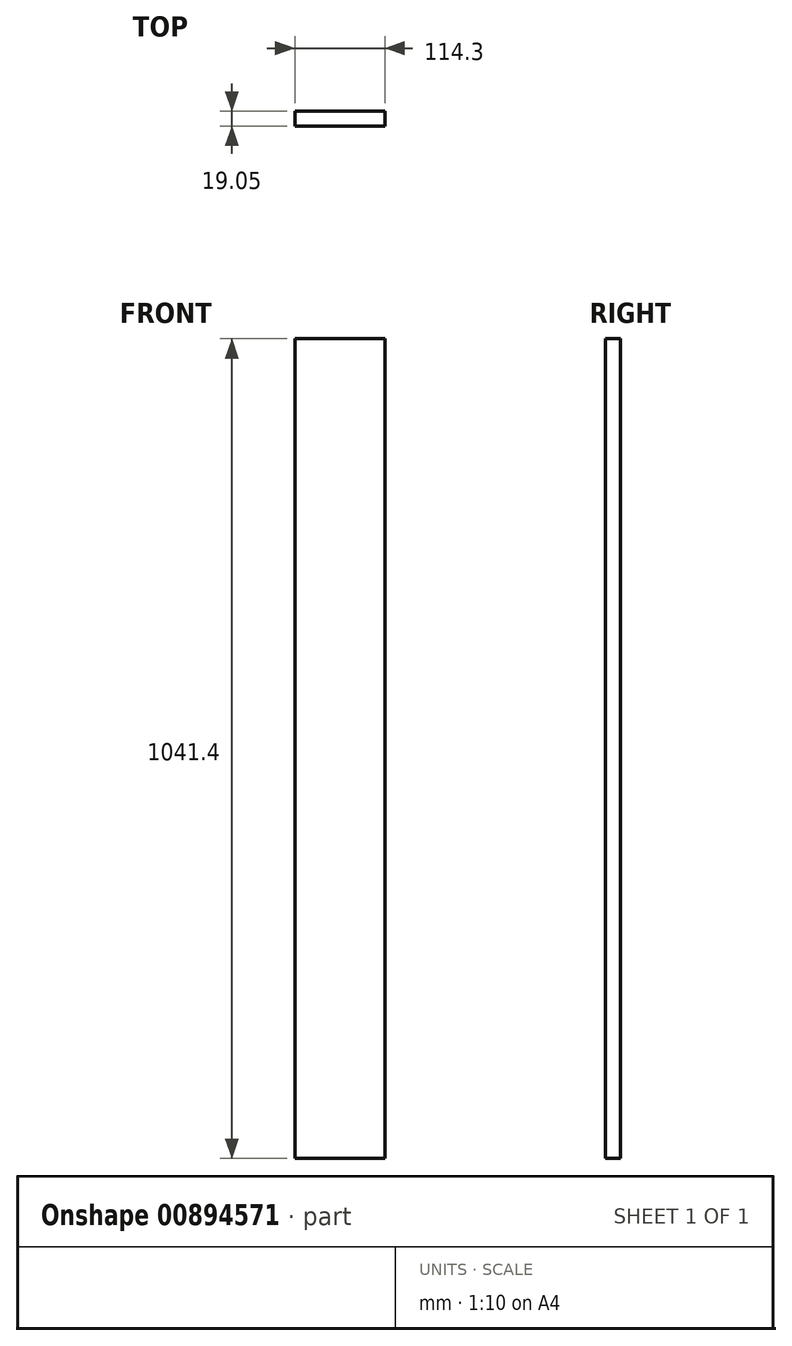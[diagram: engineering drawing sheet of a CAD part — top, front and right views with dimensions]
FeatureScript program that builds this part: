
annotation { "Feature Type Name" : "Feature", "Feature Type Description" : "" }
export const myFeature = defineFeature(function(context is Context, id is Id, definition is map)
    precondition{}
    {
        {
            var Q0;
            Q0=qCreatedBy(makeId("Front.planeOp"),FACE);
            var sketch = newSketch(context, id + "F0", { "sketchPlane" : qUnion([Q0])});
            skLineSegment(sketch, "E0.bottom", {"start": v(57.15, 520.7) * mm, "end": v(-57.15, 520.7) * mm});
            skLineSegment(sketch, "E0.top", {"start": v(57.15, -520.7) * mm, "end": v(-57.15, -520.7) * mm});
            skLineSegment(sketch, "E0.left", {"start": v(57.15, 520.7) * mm, "end": v(57.15, -520.7) * mm});
            skLineSegment(sketch, "E0.right", {"start": v(-57.15, 520.7) * mm, "end": v(-57.15, -520.7) * mm});
            skPoint(sketch, "E0.middle", {"position": v(0, 0) * mm});
            skSolve(sketch);
        }
        {
            var Q0;
            Q0=makeQuery(id+"F0.imprint","IMPRINT",FACE,{"disambiguationData":[TD([[makeQuery(id+"F0.imprint","IMPRINT",EDGE,{"derivedFrom":sQuery(id+"F0.wireOp",EDGE,"E0.bottom")}),1.0]])]});
            extrude(context, id + "F1", {"entities" : qUnion([Q0]), "depth" : 19.05 * mm, "offsetDistance" : 25.4 * mm});
        }
    });
